FCSTD DOCUMENT  (FreeCAD 0.21R33694 (Git))
Label: new_nose
License: All rights reserved
LicenseURL: http://en.wikipedia.org/wiki/All_rights_reserved
objects: Image::ImagePlane×3, Sketcher::SketchObject×3, PartDesign::Body×1
note: 4 computed .brp shape members not serialized (recipe doc carries the construction recipe); baked Part::Feature solids carry a one-line shape summary decoded from their .brp

FEATURE [Image::ImagePlane] Screenshot_from_2023_10_14_23_55_51  label="2_xsec"
  Placement = pos=(-6,0.8,0) rot=(0,0,1;0rad)
  XSize = 152.44
  YSize = 118.413
FEATURE [Image::ImagePlane] Screenshot_from_2023_10_14_23_56_05  label="1_xsec"
  Placement = pos=(-1.3,-0.1,0) rot=(0,0,1;0rad)
  XSize = 114.853
  YSize = 93.8727
FEATURE [Image::ImagePlane] Screenshot_from_2023_10_14_23_56_29  label="3_xsec"
  Placement = pos=(-8.1,5.1,0) rot=(0,0,1;0rad)
  XSize = 175.768
  YSize = 119.373
FEATURE [Sketcher::SketchObject] Sketch
  FullyConstrained = false
  MapMode = 5
  Support = -> [XY_Plane]
  sketch-geometry (22):
    g0: LineSegment StartX=0 StartY=32.0453 StartZ=0 EndX=7.04028 EndY=32.0453 EndZ=0
    g1: LineSegment StartX=0 StartY=-30.7509 StartZ=0 EndX=6.4945 EndY=-30.7509 EndZ=0
    g2: LineSegment StartX=33.4161 StartY=5.04342 StartZ=0 EndX=33.4161 EndY=-5.19902 EndZ=0
    g3-g6: Circle x4 (B-spline internal-alignment scaffolding for g7; pole/knot coordinates omitted)
    g7: BSplineCurve PolesCount=4 KnotsCount=2 Degree=3 IsPeriodic=0
    g8: GeomPoint X=7.04028 Y=32.0453 Z=0
    g9: GeomPoint X=33.4161 Y=5.04342 Z=0
    g10-g13: Circle x4 (B-spline internal-alignment scaffolding for g14; pole/knot coordinates omitted)
    g14: BSplineCurve PolesCount=4 KnotsCount=2 Degree=3 IsPeriodic=0
    g15: GeomPoint X=33.4161 Y=-5.19902 Z=0
    g16: GeomPoint X=6.4945 Y=-30.7509 Z=0
    g17: LineSegment StartX=0 StartY=32.0453 StartZ=0 EndX=-7.04028 EndY=32.0453 EndZ=0
    g18: BSplineCurve PolesCount=4 KnotsCount=2 Degree=3 IsPeriodic=0
    g19: LineSegment StartX=-33.4161 StartY=5.04342 StartZ=0 EndX=-33.4161 EndY=-5.19902 EndZ=0
    g20: BSplineCurve PolesCount=4 KnotsCount=2 Degree=3 IsPeriodic=0
    g21: LineSegment StartX=0 StartY=-30.7509 StartZ=0 EndX=-6.4945 EndY=-30.7509 EndZ=0
  constraints (30):
    c: PointOnObject(g0,g-2)
    c: Horizontal(g0)
    c: PointOnObject(g1,g-2)
    c: Horizontal(g1)
    c: Vertical(g2)
    c: Weight(g3) = 1
    c: Coincident(g7,g0)
    c: Equal(g3,g4)
    c: Equal(g3,g5)
    c: Equal(g3,g6)
    c: Coincident(g7,g2)
    c: InternalAlignment(g3-g6 -> g7) x4
    c: InternalAlignment(g8,g7)
    c: InternalAlignment(g9,g7)
    c: Weight(g10) = 1
    c: Coincident(g14,g2)
    c: Equal(g10,g11)
    c: Equal(g10,g12)
    c: Equal(g10,g13)
    c: Coincident(g14,g1)
    c: InternalAlignment(g10-g13 -> g14) x4
    c: InternalAlignment(g15,g14)
    c: InternalAlignment(g16,g14)
    c: Horizontal(g17)
    c: Horizontal(g21)
    c: Vertical(g19)
    c: Coincident(g18,g17)
    c: Coincident(g18,g19)
    c: Coincident(g20,g19)
    c: Coincident(g20,g21)
FEATURE [Sketcher::SketchObject] Sketch001
  AttachmentOffset = pos=(0,0,41) rot=(0,0,1;0rad)
  FullyConstrained = false
  MapMode = 5
  Placement = pos=(0,0,41) rot=(0,0,1;0rad)
  Support = -> [XY_Plane]
  sketch-geometry (20):
    g0: LineSegment StartX=0 StartY=36.0908 StartZ=0 EndX=5.33597 EndY=36.0908 EndZ=0
    g1: LineSegment StartX=37.3636 StartY=4.8552 StartZ=0 EndX=37.3636 EndY=-4.2167 EndZ=0
    g2: LineSegment StartX=0 StartY=-35.6514 StartZ=0 EndX=4.92976 EndY=-35.6514 EndZ=0
    g3: Circle CenterX=4.92976 CenterY=-35.6514 CenterZ=0 NormalX=0 NormalY=0 NormalZ=1 AngleXU=0 Radius=1
    g4: Circle CenterX=32.8508 CenterY=-31.0597 CenterZ=0 NormalX=0 NormalY=0 NormalZ=1 AngleXU=0 Radius=1
    g5: Circle CenterX=37.3636 CenterY=-4.2167 CenterZ=0 NormalX=0 NormalY=0 NormalZ=1 AngleXU=0 Radius=1
    g6: BSplineCurve PolesCount=3 KnotsCount=2 Degree=2 IsPeriodic=0
    g7: GeomPoint X=4.92976 Y=-35.6514 Z=0
    g8: GeomPoint X=37.3636 Y=-4.2167 Z=0
    g9: Circle CenterX=37.3636 CenterY=4.8552 CenterZ=0 NormalX=0 NormalY=0 NormalZ=1 AngleXU=0 Radius=1
    g10: Circle CenterX=32.319 CenterY=31.0668 CenterZ=0 NormalX=0 NormalY=0 NormalZ=1 AngleXU=0 Radius=1
    g11: Circle CenterX=5.33597 CenterY=36.0908 CenterZ=0 NormalX=0 NormalY=0 NormalZ=1 AngleXU=0 Radius=1
    g12: BSplineCurve PolesCount=3 KnotsCount=2 Degree=2 IsPeriodic=0
    g13: GeomPoint X=37.3636 Y=4.8552 Z=0
    g14: GeomPoint X=5.33597 Y=36.0908 Z=0
    g15: LineSegment StartX=0 StartY=36.0908 StartZ=0 EndX=-5.33597 EndY=36.0908 EndZ=0
    g16: BSplineCurve PolesCount=3 KnotsCount=2 Degree=2 IsPeriodic=0
    g17: LineSegment StartX=-37.3636 StartY=4.8552 StartZ=0 EndX=-37.3636 EndY=-4.2167 EndZ=0
    g18: BSplineCurve PolesCount=3 KnotsCount=2 Degree=2 IsPeriodic=0
    g19: LineSegment StartX=0 StartY=-35.6514 StartZ=0 EndX=-4.92976 EndY=-35.6514 EndZ=0
  constraints (32):
    c: PointOnObject(g0,g-2)
    c: Horizontal(g0)
    c: Vertical(g1)
    c: PointOnObject(g2,g-2)
    c: Horizontal(g2)
    c: Weight(g3) = 1
    c: Coincident(g6,g2)
    c: Equal(g3,g4)
    c: Equal(g3,g5)
    c: Coincident(g6,g1)
    c: InternalAlignment(g3,g6)
    c: InternalAlignment(g4,g6)
    c: InternalAlignment(g5,g6)
    c: InternalAlignment(g7,g6)
    c: InternalAlignment(g8,g6)
    c: Weight(g9) = 1
    c: Coincident(g12,g1)
    c: Equal(g9,g10)
    c: Equal(g9,g11)
    c: Coincident(g12,g0)
    c: InternalAlignment(g9,g12)
    c: InternalAlignment(g10,g12)
    c: InternalAlignment(g11,g12)
    c: InternalAlignment(g13,g12)
    c: InternalAlignment(g14,g12)
    c: Horizontal(g15)
    c: Vertical(g17)
    c: Horizontal(g19)
    c: Coincident(g18,g19)
    c: Coincident(g18,g17)
    c: Coincident(g16,g17)
    c: Coincident(g16,g15)
FEATURE [Sketcher::SketchObject] Sketch002
  AttachmentOffset = pos=(0,0,80) rot=(0,0,1;0rad)
  FullyConstrained = false
  MapMode = 5
  Placement = pos=(0,0,80) rot=(0,0,1;0rad)
  Support = -> [XY_Plane]
  sketch-geometry (22):
    g0: LineSegment StartX=0 StartY=51.6621 StartZ=0 EndX=10.1339 EndY=51.6621 EndZ=0
    g1: LineSegment StartX=0 StartY=-36.6829 StartZ=0 EndX=7.57249 EndY=-36.6829 EndZ=0
    g2-g10: Circle x9 (B-spline internal-alignment scaffolding for g11; pole/knot coordinates omitted)
    g11: BSplineCurve PolesCount=9 KnotsCount=7 Degree=3 IsPeriodic=0
    g12-g18: GeomPoint x7 (B-spline internal-alignment scaffolding for g11; pole/knot coordinates omitted)
    g19: LineSegment StartX=0 StartY=-36.6829 StartZ=0 EndX=-7.57249 EndY=-36.6829 EndZ=0
    g20: BSplineCurve PolesCount=9 KnotsCount=7 Degree=3 IsPeriodic=0
    g21: LineSegment StartX=0 StartY=51.6621 StartZ=0 EndX=-10.1339 EndY=51.6621 EndZ=0
  constraints (16):
    c: PointOnObject(g0,g-2)
    c: Horizontal(g0)
    c: PointOnObject(g1,g-2)
    c: Horizontal(g1)
    c: Weight(g2) = 1
    c: Coincident(g11,g1)
    c: Equal(g2, g3-g6) x4
    c: PointOnObject(g6,g-1)
    c: Equal(g2, g7-g10) x4
    c: Coincident(g11,g0)
    c: InternalAlignment(g2-g10 -> g11) x9
    c: InternalAlignment(g12-g18 -> g11) x7
    c: Horizontal(g21)
    c: Horizontal(g19)
    c: Coincident(g20,g19)
    c: Coincident(g20,g21)
FEATURE [PartDesign::Body] Body
  Group = -> [Sketch,Sketch001,Sketch002]
  Origin = -> Origin
